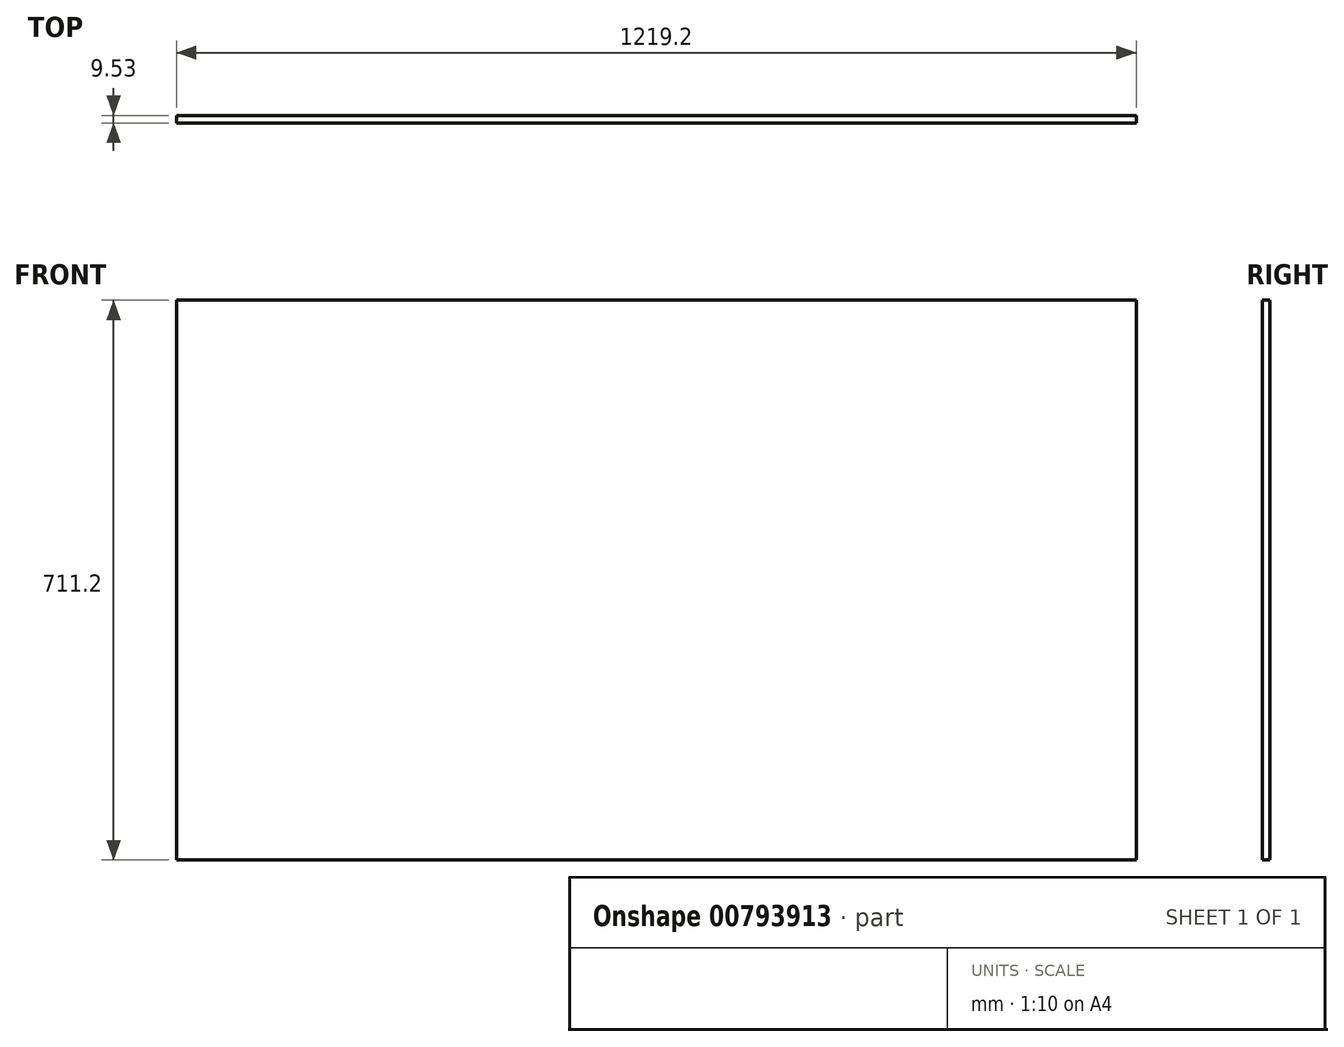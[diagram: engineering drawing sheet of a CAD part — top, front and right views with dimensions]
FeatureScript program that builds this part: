
annotation { "Feature Type Name" : "Feature", "Feature Type Description" : "" }
export const myFeature = defineFeature(function(context is Context, id is Id, definition is map)
    precondition{}
    {
        {
            var Q0;
            Q0=qCreatedBy(makeId("Front.planeOp"),FACE);
            var sketch = newSketch(context, id + "F0", { "sketchPlane" : qUnion([Q0])});
            skLineSegment(sketch, "E0.bottom", {"start": v(609.6, 355.6) * mm, "end": v(-609.6, 355.6) * mm});
            skLineSegment(sketch, "E0.top", {"start": v(609.6, -355.6) * mm, "end": v(-609.6, -355.6) * mm});
            skLineSegment(sketch, "E0.left", {"start": v(609.6, 355.6) * mm, "end": v(609.6, -355.6) * mm});
            skLineSegment(sketch, "E0.right", {"start": v(-609.6, 355.6) * mm, "end": v(-609.6, -355.6) * mm});
            skPoint(sketch, "E0.middle", {"position": v(0, 0) * mm});
            skSolve(sketch);
        }
        {
            var Q0;
            Q0=makeQuery(id+"F0.imprint","IMPRINT",FACE,{"disambiguationData":[TD([[makeQuery(id+"F0.imprint","IMPRINT",EDGE,{"derivedFrom":sQuery(id+"F0.wireOp",EDGE,"E0.bottom")}),1.0]])]});
            extrude(context, id + "F1", {"entities" : qUnion([Q0]), "oppositeDirection" : true, "depth" : 9.52 * mm, "offsetDistance" : 25.4 * mm});
        }
    });
